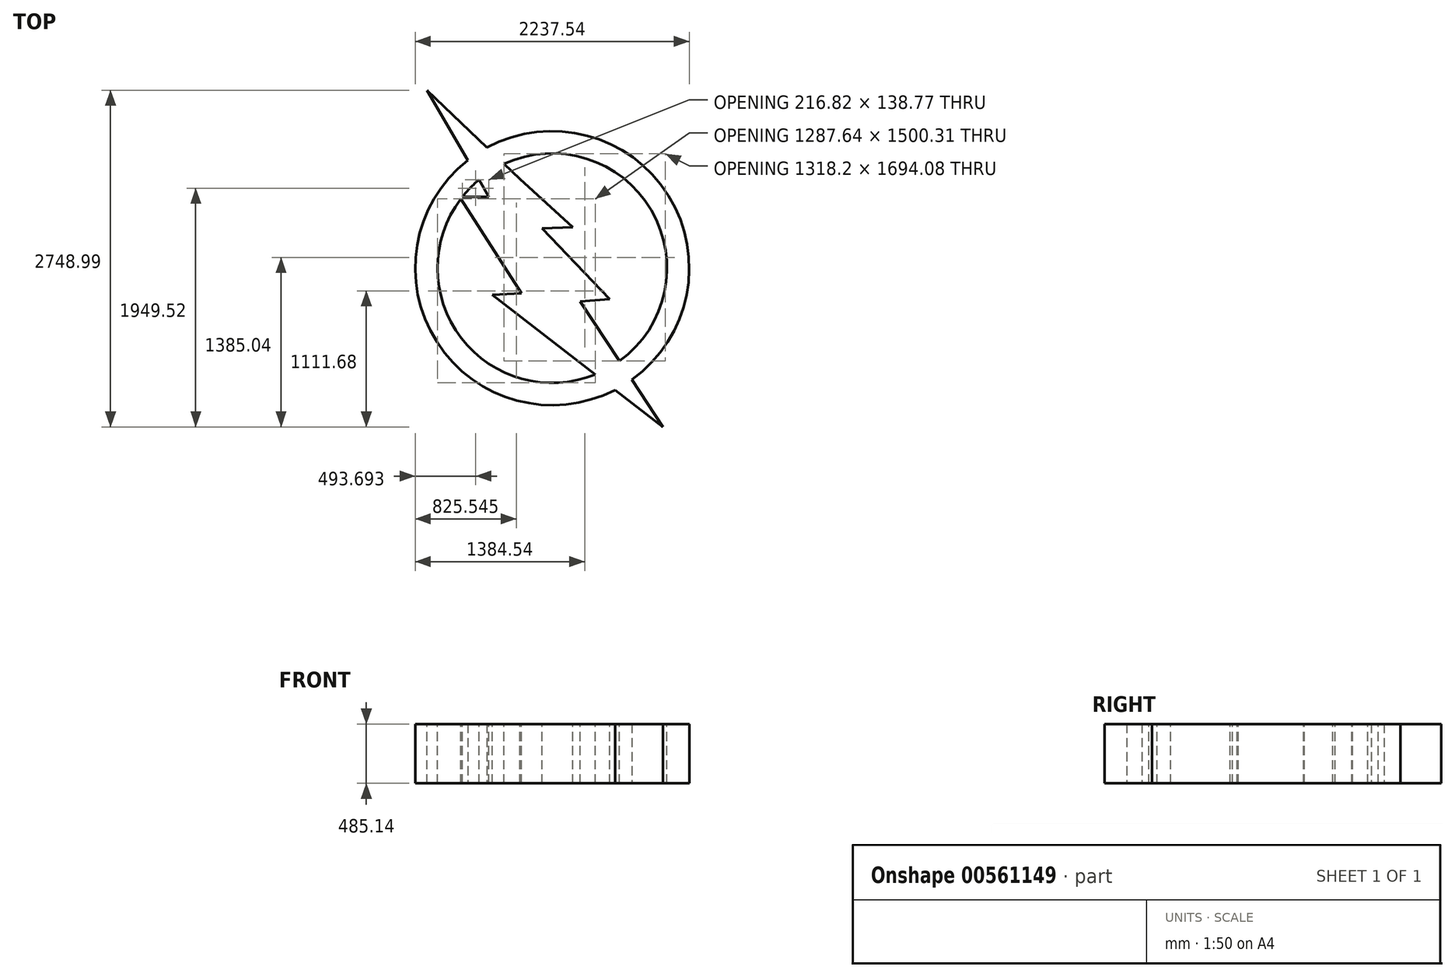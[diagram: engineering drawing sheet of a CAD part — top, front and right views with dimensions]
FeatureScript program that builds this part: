
annotation { "Feature Type Name" : "Feature", "Feature Type Description" : "" }
export const myFeature = defineFeature(function(context is Context, id is Id, definition is map)
    precondition{}
    {
        {
            var Q0;
            Q0=qCreatedBy(makeId("Top.planeOp"),FACE);
            var sketch = newSketch(context, id + "F0", { "sketchPlane" : qUnion([Q0])});
            skCircle(sketch, "E0", {"center": v(-116.98, 21.37) * mm, "radius": 1118.77 * mm});
            skSolve(sketch);
        }
        {
            var Q0;
            Q0 = qSketchRegion(id + "F0", true);
            extrude(context, id + "F1", {"entities" : qUnion([Q0]), "depth" : 485.14 * mm, "offsetDistance" : 25.4 * mm});
        }
        {
            var Q0;
            Q0=makeQuery(id+"F1.opExtrude","CAP_FACE",FACE,{"disambiguationData":[OSD([sQuery(id+"F0.wireOp",EDGE,"E0")])],"isStart":false});
            var sketch = newSketch(context, id + "F2", { "sketchPlane" : qUnion([Q0])});
            skCircle(sketch, "E1", {"center": v(-116.98, 21.37) * mm, "radius": 937.05 * mm});
            skSolve(sketch);
        }
        {
            var Q0;
            Q0=makeQuery(id+"F2.imprint","IMPRINT",FACE,{"disambiguationData":[TD([[makeQuery(id+"F2.imprint","IMPRINT",EDGE,{"derivedFrom":sQuery(id+"F2.wireOp",EDGE,"E1")}),1.0]])]});
            extrude(context, id + "F3", {"entities" : qUnion([Q0]), "operationType" : NewBodyOperationType.REMOVE, "endBound" : BoundingType.THROUGH_ALL, "oppositeDirection" : true, "depth" : 25.4 * mm, "offsetDistance" : 25.4 * mm});
        }
        {
            var Q0;
            Q0=makeQuery(id+"F1.opExtrude","CAP_FACE",FACE,{"disambiguationData":[OSD([sQuery(id+"F0.wireOp",EDGE,"E0")])],"isStart":false});
            var sketch = newSketch(context, id + "F4", { "sketchPlane" : qUnion([Q0])});
            skLineSegment(sketch, "E2", {"start": v(-1139.13, 1473.37) * mm, "end": v(-381.4, 748.55) * mm});
            skLineSegment(sketch, "E3", {"start": v(-381.4, 748.55) * mm, "end": v(51.2, 354.34) * mm});
            skLineSegment(sketch, "E4", {"start": v(51.2, 354.34) * mm, "end": v(-198.45, 347.4) * mm});
            skLineSegment(sketch, "E5", {"start": v(-198.45, 347.4) * mm, "end": v(353.64, -231.87) * mm});
            skLineSegment(sketch, "E6", {"start": v(353.64, -231.87) * mm, "end": v(112.3, -250.2) * mm});
            skLineSegment(sketch, "E7", {"start": v(112.3, -250.2) * mm, "end": v(786.03, -1275.62) * mm});
            skLineSegment(sketch, "E8", {"start": v(786.03, -1275.62) * mm, "end": v(-607.88, -195.67) * mm});
            skLineSegment(sketch, "E9", {"start": v(-607.88, -195.67) * mm, "end": v(-369.62, -183.48) * mm});
            skLineSegment(sketch, "E10", {"start": v(-369.62, -183.48) * mm, "end": v(-876.4, 604.51) * mm});
            skLineSegment(sketch, "E11", {"start": v(-876.4, 604.51) * mm, "end": v(-633.65, 604.51) * mm});
            skLineSegment(sketch, "E12", {"start": v(-633.65, 604.51) * mm, "end": v(-1139.13, 1473.37) * mm});
            skSolve(sketch);
        }
        {
            var Q0;
            Q0 = qSketchRegion(id + "F4", true);
            extrude(context, id + "F5", {"entities" : qUnion([Q0]), "operationType" : NewBodyOperationType.ADD, "oppositeDirection" : true, "depth" : 485.14 * mm, "offsetDistance" : 25.4 * mm});
        }
    });
